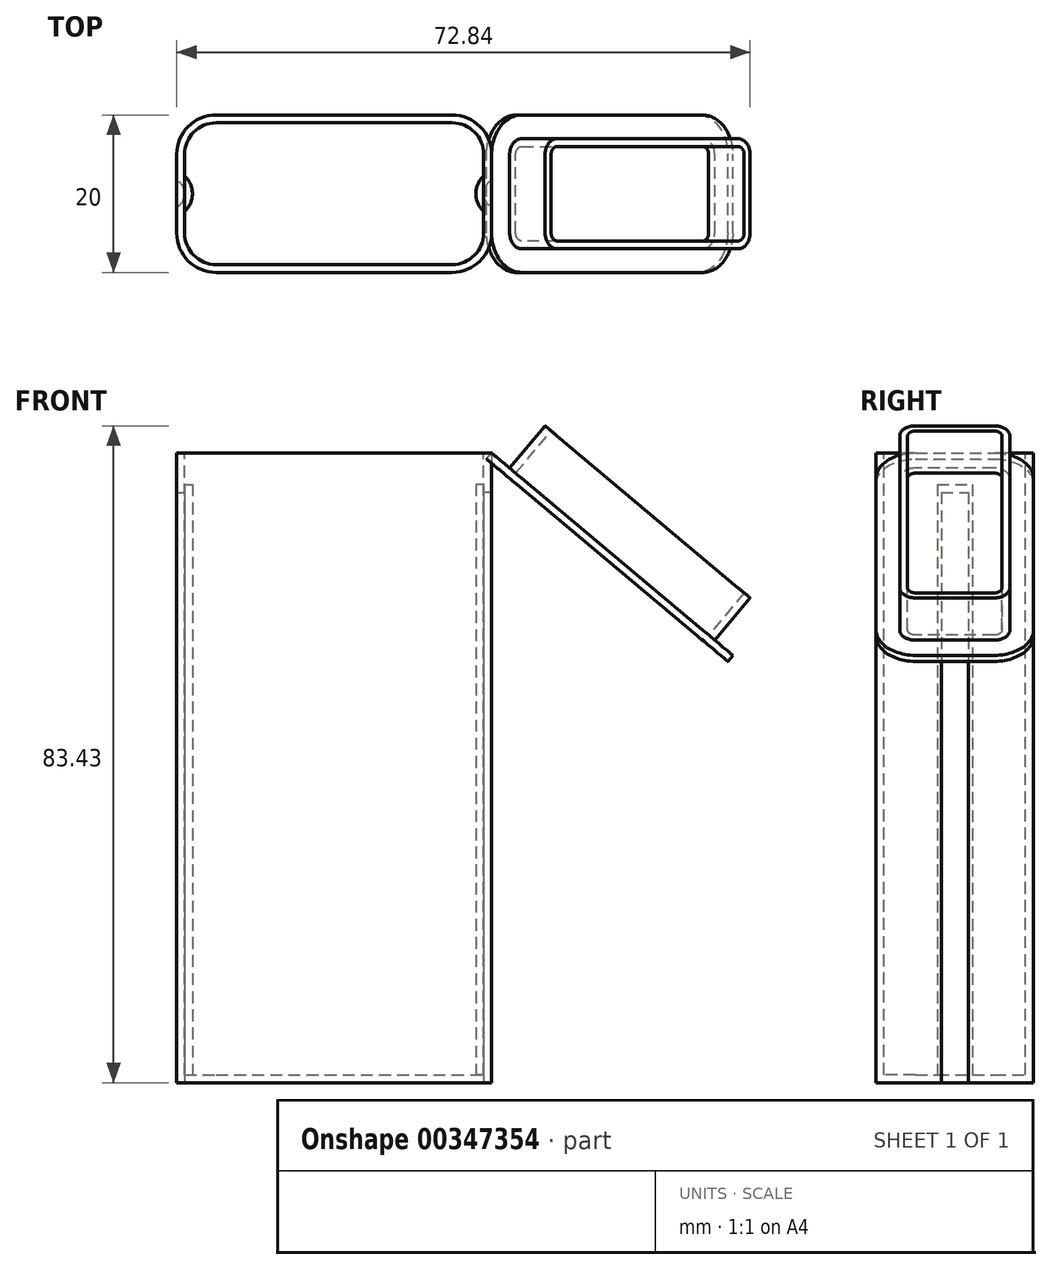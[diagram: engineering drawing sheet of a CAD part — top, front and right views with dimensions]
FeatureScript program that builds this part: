
annotation { "Feature Type Name" : "Feature", "Feature Type Description" : "" }
export const myFeature = defineFeature(function(context is Context, id is Id, definition is map)
    precondition{}
    {
        {
            var Q0;
            Q0=qCreatedBy(makeId("Top.planeOp"),FACE);
            var sketch = newSketch(context, id + "F0", { "sketchPlane" : qUnion([Q0])});
            skLineSegment(sketch, "E0.bottom", {"start": v(0, 0) * mm, "end": v(40, 0) * mm});
            skLineSegment(sketch, "E0.top", {"start": v(0, 20) * mm, "end": v(40, 20) * mm});
            skLineSegment(sketch, "E0.left", {"start": v(0, 0) * mm, "end": v(0, 20) * mm});
            skLineSegment(sketch, "E0.right", {"start": v(40, 0) * mm, "end": v(40, 20) * mm});
            skSolve(sketch);
        }
        {
            var Q0;
            Q0 = qSketchRegion(id + "F0", true);
            extrude(context, id + "F1", {"entities" : qUnion([Q0]), "depth" : 80 * mm});
        }
        {
            var Q0;
            Q0=makeQuery(id+"F1.opExtrude","SWEPT_EDGE",EDGE,{"disambiguationData":[OSD([sQuery(id+"F0.wireOp",EDGE,"E0.bottom"),sQuery(id+"F0.wireOp",EDGE,"E0.right")])]});
            var Q1;
            Q1=makeQuery(id+"F1.opExtrude","SWEPT_EDGE",EDGE,{"disambiguationData":[OSD([sQuery(id+"F0.wireOp",EDGE,"E0.bottom"),sQuery(id+"F0.wireOp",EDGE,"E0.left")])]});
            var Q2;
            Q2=makeQuery(id+"F1.opExtrude","SWEPT_EDGE",EDGE,{"disambiguationData":[OSD([sQuery(id+"F0.wireOp",EDGE,"E0.top"),sQuery(id+"F0.wireOp",EDGE,"E0.right")])]});
            var Q3;
            Q3=makeQuery(id+"F1.opExtrude","SWEPT_EDGE",EDGE,{"disambiguationData":[OSD([sQuery(id+"F0.wireOp",EDGE,"E0.top"),sQuery(id+"F0.wireOp",EDGE,"E0.left")])]});
            fillet(context, id + "F2", {"entities" : qUnion([Q0, Q1, Q2, Q3]), "radius" : 5 * mm, "tangentPropagation" : true, "allowEdgeOverflow" : false});
        }
        {
            var Q0;
            Q0=makeQuery(id+"F1.opExtrude","CAP_FACE",FACE,{"disambiguationData":[OSD([sQuery(id+"F0.wireOp",EDGE,"E0.bottom"),sQuery(id+"F0.wireOp",EDGE,"E0.top"),sQuery(id+"F0.wireOp",EDGE,"E0.left"),sQuery(id+"F0.wireOp",EDGE,"E0.right")])],"isStart":true});
            var sketch = newSketch(context, id + "F3", { "sketchPlane" : qUnion([Q0])});
            skArc(sketch, "E1", {"start": v(0, -11.73) * mm, "mid": v(1, -10) * mm, "end": v(0, -8.27) * mm});
            skLineSegment(sketch, "E2", {"start": v(20, 0) * mm, "end": v(20, -20) * mm, "construction": true});
            skLineSegment(sketch, "E3", {"start": v(0, -10) * mm, "end": v(20, -10) * mm, "construction": true});
            skLineSegment(sketch, "E4", {"start": v(0, -8.27) * mm, "end": v(0, -11.73) * mm});
            skArc(sketch, "E5.MirrorCS", {"start": v(40, -11.73) * mm, "mid": v(39, -10) * mm, "end": v(40, -8.27) * mm});
            skLineSegment(sketch, "E6.MirrorCS", {"start": v(40, -8.27) * mm, "end": v(40, -11.73) * mm});
            skSolve(sketch);
        }
        {
            var Q0;
            Q0 = qSketchRegion(id + "F3", true);
            extrude(context, id + "F4", {"entities" : qUnion([Q0]), "operationType" : NewBodyOperationType.REMOVE, "oppositeDirection" : true, "depth" : 75 * mm});
        }
        {
            var Q0;
            Q0=makeQuery(id+"F1.opExtrude","CAP_FACE",FACE,{"disambiguationData":[OSD([sQuery(id+"F0.wireOp",EDGE,"E0.bottom"),sQuery(id+"F0.wireOp",EDGE,"E0.top"),sQuery(id+"F0.wireOp",EDGE,"E0.left"),sQuery(id+"F0.wireOp",EDGE,"E0.right")])],"isStart":false});
            shell(context, id + "F5", {"entities" : qUnion([Q0]), "thickness" : 1 * mm});
        }
        {
            var Q0;
            Q0=makeQuery(id+"F1.opExtrude","CAP_FACE",FACE,{"disambiguationData":[OSD([sQuery(id+"F0.wireOp",EDGE,"E0.bottom"),sQuery(id+"F0.wireOp",EDGE,"E0.top"),sQuery(id+"F0.wireOp",EDGE,"E0.left"),sQuery(id+"F0.wireOp",EDGE,"E0.right")])],"isStart":false});
            var sketch = newSketch(context, id + "F6", { "sketchPlane" : qUnion([Q0])});
            skLineSegment(sketch, "E7.0", {"start": v(40, 5) * mm, "end": v(40, 15) * mm});
            skPoint(sketch, "E8.0", {"position": v(38.54, 1.46) * mm});
            skArc(sketch, "E9.0", {"start": v(35, 0) * mm, "mid": v(38.54, 1.46) * mm, "end": v(40, 5) * mm});
            skLineSegment(sketch, "E10.0", {"start": v(5, 0) * mm, "end": v(35, 0) * mm});
            skArc(sketch, "E11.0", {"start": v(0, 5) * mm, "mid": v(1.46, 1.46) * mm, "end": v(5, 0) * mm});
            skLineSegment(sketch, "E12.0", {"start": v(0, 5) * mm, "end": v(0, 15) * mm});
            skArc(sketch, "E13.0", {"start": v(5, 20) * mm, "mid": v(1.46, 18.54) * mm, "end": v(0, 15) * mm});
            skLineSegment(sketch, "E14.0", {"start": v(5, 20) * mm, "end": v(35, 20) * mm});
            skArc(sketch, "E15.0", {"start": v(40, 15) * mm, "mid": v(38.54, 18.54) * mm, "end": v(35, 20) * mm});
            skSolve(sketch);
        }
        {
            var Q0;
            Q0 = qSketchRegion(id + "F6", true);
            extrude(context, id + "F7", {"entities" : qUnion([Q0]), "depth" : 8 * mm});
        }
        {
            var Q0;
            Q0=makeQuery(id+"F7.opExtrude","SWEPT_BODY",BODY,{"disambiguationData":[OSD([sQuery(id+"F6.wireOp",EDGE,"E7.0"),sQuery(id+"F6.wireOp",EDGE,"E9.0"),sQuery(id+"F6.wireOp",EDGE,"E10.0"),sQuery(id+"F6.wireOp",EDGE,"E11.0"),sQuery(id+"F6.wireOp",EDGE,"E12.0"),sQuery(id+"F6.wireOp",EDGE,"E13.0"),sQuery(id+"F6.wireOp",EDGE,"E14.0"),sQuery(id+"F6.wireOp",EDGE,"E15.0")])]});
            var Q1;
            Q1=makeQuery(id+"F1.opExtrude","CAP_EDGE",EDGE,{"disambiguationData":[OSD([sQuery(id+"F0.wireOp",EDGE,"E0.right")])],"isStart":false});
            var Q2;
            Q2=makeQuery(id+"F1.opExtrude","CAP_EDGE",EDGE,{"disambiguationData":[OSD([sQuery(id+"F0.wireOp",EDGE,"E0.right")])],"isStart":false});
            transform(context, id + "F8", {"entities" : qUnion([Q0]), "transformType" : TransformType.ROTATION, "transformAxis" : qUnion([Q2]), "angle" : 220 * degree, "makeCopy" : false});
        }
        {
            var Q0;
            Q0=makeQuery(id+"F7.opExtrude","SWEPT_BODY",BODY,{"disambiguationData":[OSD([sQuery(id+"F6.wireOp",EDGE,"E7.0"),sQuery(id+"F6.wireOp",EDGE,"E9.0"),sQuery(id+"F6.wireOp",EDGE,"E10.0"),sQuery(id+"F6.wireOp",EDGE,"E11.0"),sQuery(id+"F6.wireOp",EDGE,"E12.0"),sQuery(id+"F6.wireOp",EDGE,"E13.0"),sQuery(id+"F6.wireOp",EDGE,"E14.0"),sQuery(id+"F6.wireOp",EDGE,"E15.0")])]});
            var Q1;
            Q1=makeQuery(id+"F7.opExtrude","SWEPT_EDGE",EDGE,{"disambiguationData":[OSD([sQuery(id+"F6.wireOp",EDGE,"E14.0"),sQuery(id+"F6.wireOp",EDGE,"E15.0")])]});
            transform(context, id + "F9", {"entities" : qUnion([Q0]), "transformType" : TransformType.TRANSLATION_DISTANCE, "transformDirection" : qUnion([Q1]), "distance" : 7 * mm, "makeCopy" : false});
        }
        {
            var Q0;
            Q0=makeQuery(id+"F7.opExtrude","CAP_FACE",FACE,{"disambiguationData":[OSD([sQuery(id+"F6.wireOp",EDGE,"E7.0"),sQuery(id+"F6.wireOp",EDGE,"E9.0"),sQuery(id+"F6.wireOp",EDGE,"E10.0"),sQuery(id+"F6.wireOp",EDGE,"E11.0"),sQuery(id+"F6.wireOp",EDGE,"E12.0"),sQuery(id+"F6.wireOp",EDGE,"E13.0"),sQuery(id+"F6.wireOp",EDGE,"E14.0"),sQuery(id+"F6.wireOp",EDGE,"E15.0")])],"isStart":true});
            var sketch = newSketch(context, id + "F10", { "sketchPlane" : qUnion([Q0])});
            skLineSegment(sketch, "E16.0.0", {"start": v(14.22, 20) * mm, "end": v(-15.78, 20) * mm});
            skArc(sketch, "E16.0.1", {"start": v(-15.78, 20) * mm, "mid": v(-19.32, 18.54) * mm, "end": v(-20.78, 15) * mm});
            skLineSegment(sketch, "E16.0.2", {"start": v(-20.78, 15) * mm, "end": v(-20.78, 5) * mm});
            skArc(sketch, "E16.0.3", {"start": v(-20.78, 5) * mm, "mid": v(-19.32, 1.46) * mm, "end": v(-15.78, 0) * mm});
            skLineSegment(sketch, "E16.0.4", {"start": v(-15.78, 0) * mm, "end": v(14.22, 0) * mm});
            skArc(sketch, "E16.0.5", {"start": v(14.22, 0) * mm, "mid": v(17.75, 1.46) * mm, "end": v(19.22, 5) * mm});
            skLineSegment(sketch, "E16.0.6", {"start": v(19.22, 5) * mm, "end": v(19.22, 15) * mm});
            skArc(sketch, "E16.0.7", {"start": v(19.22, 15) * mm, "mid": v(17.75, 18.54) * mm, "end": v(14.22, 20) * mm});
            skArc(sketch, "E17.0", {"start": v(16.22, 15) * mm, "mid": v(15.63, 16.41) * mm, "end": v(14.22, 17) * mm});
            skLineSegment(sketch, "E17.1", {"start": v(16.22, 5) * mm, "end": v(16.22, 15) * mm});
            skLineSegment(sketch, "E17.2", {"start": v(14.22, 17) * mm, "end": v(-15.78, 17) * mm});
            skArc(sketch, "E17.3", {"start": v(14.22, 3) * mm, "mid": v(15.63, 3.59) * mm, "end": v(16.22, 5) * mm});
            skArc(sketch, "E17.4", {"start": v(-15.78, 17) * mm, "mid": v(-17.2, 16.41) * mm, "end": v(-17.78, 15) * mm});
            skLineSegment(sketch, "E17.5", {"start": v(-17.78, 15) * mm, "end": v(-17.78, 5) * mm});
            skArc(sketch, "E17.6", {"start": v(-17.78, 5) * mm, "mid": v(-17.2, 3.59) * mm, "end": v(-15.78, 3) * mm});
            skLineSegment(sketch, "E17.7", {"start": v(-15.78, 3) * mm, "end": v(14.22, 3) * mm});
            skArc(sketch, "E18.0", {"start": v(15.22, 15) * mm, "mid": v(14.93, 15.7) * mm, "end": v(14.22, 16) * mm});
            skLineSegment(sketch, "E18.1", {"start": v(15.22, 5) * mm, "end": v(15.22, 15) * mm});
            skLineSegment(sketch, "E18.2", {"start": v(14.22, 16) * mm, "end": v(-15.78, 16) * mm});
            skArc(sketch, "E18.3", {"start": v(14.22, 4) * mm, "mid": v(14.93, 4.3) * mm, "end": v(15.22, 5) * mm});
            skArc(sketch, "E18.4", {"start": v(-15.78, 16) * mm, "mid": v(-16.49, 15.7) * mm, "end": v(-16.78, 15) * mm});
            skLineSegment(sketch, "E18.5", {"start": v(-16.78, 15) * mm, "end": v(-16.78, 5) * mm});
            skArc(sketch, "E18.6", {"start": v(-16.78, 5) * mm, "mid": v(-16.49, 4.3) * mm, "end": v(-15.78, 4) * mm});
            skLineSegment(sketch, "E18.7", {"start": v(-15.78, 4) * mm, "end": v(14.22, 4) * mm});
            skSolve(sketch);
        }
        {
            var Q0;
            Q0 = qSketchRegion(id + "F10", true);
            extrude(context, id + "F11", {"entities" : qUnion([Q0]), "operationType" : NewBodyOperationType.REMOVE, "oppositeDirection" : true, "depth" : 7 * mm});
        }
        {
            var Q0;
            Q0=makeQuery(id+"F7.opExtrude","CAP_FACE",FACE,{"disambiguationData":[OSD([sQuery(id+"F6.wireOp",EDGE,"E7.0"),sQuery(id+"F6.wireOp",EDGE,"E9.0"),sQuery(id+"F6.wireOp",EDGE,"E10.0"),sQuery(id+"F6.wireOp",EDGE,"E11.0"),sQuery(id+"F6.wireOp",EDGE,"E12.0"),sQuery(id+"F6.wireOp",EDGE,"E13.0"),sQuery(id+"F6.wireOp",EDGE,"E14.0"),sQuery(id+"F6.wireOp",EDGE,"E15.0")])],"isStart":true});
            shell(context, id + "F12", {"entities" : qUnion([Q0]), "thickness" : 1 * mm});
        }
    });
